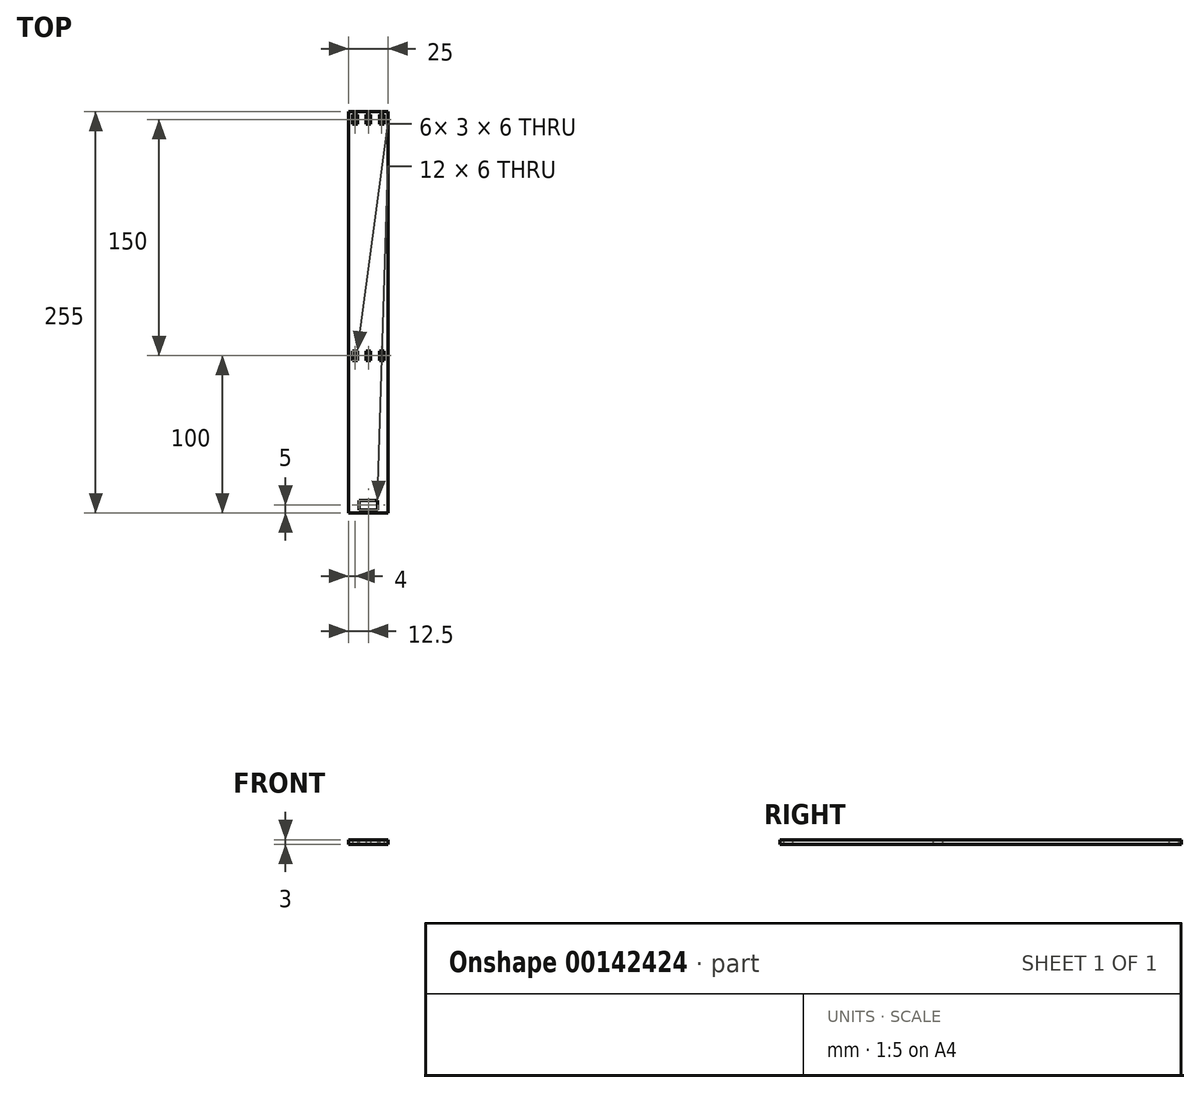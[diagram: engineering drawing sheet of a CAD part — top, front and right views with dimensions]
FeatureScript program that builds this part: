
annotation { "Feature Type Name" : "Feature", "Feature Type Description" : "" }
export const myFeature = defineFeature(function(context is Context, id is Id, definition is map)
    precondition{}
    {
        {
            var Q0;
            Q0=qCreatedBy(makeId("Top.planeOp"),FACE);
            var sketch = newSketch(context, id + "F0", { "sketchPlane" : qUnion([Q0])});
            skLineSegment(sketch, "E0", {"start": v(-12.5, 0) * mm, "end": v(-12.5, -98) * mm});
            skLineSegment(sketch, "E1", {"start": v(12.5, -98) * mm, "end": v(12.5, 0) * mm});
            skLineSegment(sketch, "E2", {"start": v(0, 0) * mm, "end": v(0, -98) * mm, "construction": true});
            skLineSegment(sketch, "E3", {"start": v(-12.5, 0) * mm, "end": v(-12.5, 7) * mm});
            skLineSegment(sketch, "E4", {"start": v(12.5, 7) * mm, "end": v(12.5, 0) * mm});
            skLineSegment(sketch, "E5", {"start": v(0, 7) * mm, "end": v(0, 5) * mm, "construction": true});
            skPoint(sketch, "E5.endSnap0", {"position": v(0, 7) * mm});
            skLineSegment(sketch, "E6", {"start": v(0, 5) * mm, "end": v(-10, 5) * mm, "construction": true});
            skLineSegment(sketch, "E7", {"start": v(-10, 5) * mm, "end": v(10, 5) * mm, "construction": true});
            skLineSegment(sketch, "E8.bottom", {"start": v(-10, 5) * mm, "end": v(-7, 5) * mm});
            skLineSegment(sketch, "E8.top", {"start": v(-10, -1) * mm, "end": v(-7, -1) * mm});
            skLineSegment(sketch, "E8.left", {"start": v(-10, 5) * mm, "end": v(-10, -1) * mm});
            skLineSegment(sketch, "E8.right", {"start": v(-7, 5) * mm, "end": v(-7, -1) * mm});
            skLineSegment(sketch, "E9", {"start": v(-7, 5) * mm, "end": v(-1.5, 5) * mm, "construction": true});
            skLineSegment(sketch, "E10.bottom", {"start": v(-1.5, 5) * mm, "end": v(1.5, 5) * mm});
            skLineSegment(sketch, "E10.top", {"start": v(-1.5, -1) * mm, "end": v(1.5, -1) * mm});
            skLineSegment(sketch, "E10.left", {"start": v(-1.5, 5) * mm, "end": v(-1.5, -1) * mm});
            skLineSegment(sketch, "E10.right", {"start": v(1.5, 5) * mm, "end": v(1.5, -1) * mm});
            skLineSegment(sketch, "E11.bottom", {"start": v(10, 5) * mm, "end": v(7, 5) * mm});
            skLineSegment(sketch, "E11.top", {"start": v(10, -1) * mm, "end": v(7, -1) * mm});
            skLineSegment(sketch, "E11.left", {"start": v(10, 5) * mm, "end": v(10, -1) * mm});
            skLineSegment(sketch, "E11.right", {"start": v(7, 5) * mm, "end": v(7, -1) * mm});
            skLineSegment(sketch, "E12", {"start": v(10, -1) * mm, "end": v(10, 157) * mm, "construction": true});
            skLineSegment(sketch, "E13", {"start": v(10, 157) * mm, "end": v(10, 155) * mm, "construction": true});
            skLineSegment(sketch, "E14.bottom", {"start": v(10, 155) * mm, "end": v(7, 155) * mm});
            skLineSegment(sketch, "E14.top", {"start": v(10, 149) * mm, "end": v(7, 149) * mm});
            skLineSegment(sketch, "E14.left", {"start": v(10, 155) * mm, "end": v(10, 149) * mm});
            skLineSegment(sketch, "E14.right", {"start": v(7, 155) * mm, "end": v(7, 149) * mm});
            skLineSegment(sketch, "E15", {"start": v(7, 155) * mm, "end": v(1.5, 155) * mm, "construction": true});
            skLineSegment(sketch, "E16.bottom", {"start": v(1.5, 155) * mm, "end": v(-1.5, 155) * mm});
            skLineSegment(sketch, "E16.top", {"start": v(1.5, 149) * mm, "end": v(-1.5, 149) * mm});
            skLineSegment(sketch, "E16.left", {"start": v(1.5, 155) * mm, "end": v(1.5, 149) * mm});
            skLineSegment(sketch, "E16.right", {"start": v(-1.5, 155) * mm, "end": v(-1.5, 149) * mm});
            skLineSegment(sketch, "E17", {"start": v(-1.5, 155) * mm, "end": v(-7, 155) * mm, "construction": true});
            skLineSegment(sketch, "E18.bottom", {"start": v(-7, 155) * mm, "end": v(-10, 155) * mm});
            skLineSegment(sketch, "E18.top", {"start": v(-7, 149) * mm, "end": v(-10, 149) * mm});
            skLineSegment(sketch, "E18.left", {"start": v(-7, 155) * mm, "end": v(-7, 149) * mm});
            skLineSegment(sketch, "E18.right", {"start": v(-10, 155) * mm, "end": v(-10, 149) * mm});
            skLineSegment(sketch, "E19", {"start": v(-12.5, 7) * mm, "end": v(-12.5, 157) * mm});
            skLineSegment(sketch, "E20", {"start": v(-12.5, 157) * mm, "end": v(10, 157) * mm});
            skLineSegment(sketch, "E21", {"start": v(12.5, 7) * mm, "end": v(12.5, 157) * mm});
            skLineSegment(sketch, "E22", {"start": v(12.5, 157) * mm, "end": v(10, 157) * mm});
            skLineSegment(sketch, "E23", {"start": v(0, -90) * mm, "end": v(6, -90) * mm});
            skLineSegment(sketch, "E24", {"start": v(6, -90) * mm, "end": v(-6, -90) * mm});
            skLineSegment(sketch, "E25", {"start": v(-6, -90) * mm, "end": v(-6, -96) * mm});
            skLineSegment(sketch, "E26", {"start": v(-6, -96) * mm, "end": v(6, -96) * mm});
            skLineSegment(sketch, "E27", {"start": v(6, -96) * mm, "end": v(6, -90) * mm});
            skLineSegment(sketch, "E28", {"start": v(-12.5, -98) * mm, "end": v(12.5, -98) * mm});
            skLineSegment(sketch, "E29.trimOffspring", {"start": v(0, -98) * mm, "end": v(0, -90) * mm, "construction": true});
            skSolve(sketch);
        }
        {
            var Q0;
            Q0=makeQuery(id+"F0.imprint","IMPRINT",FACE,{"disambiguationData":[TD([[makeQuery(id+"F0.imprint","IMPRINT",EDGE,{"derivedFrom":sQuery(id+"F0.wireOp",EDGE,"E0")}),1.0]])]});
            extrude(context, id + "F1", {"entities" : qUnion([Q0]), "endBound" : BoundingType.SYMMETRIC, "depth" : 3 * mm});
        }
    });
